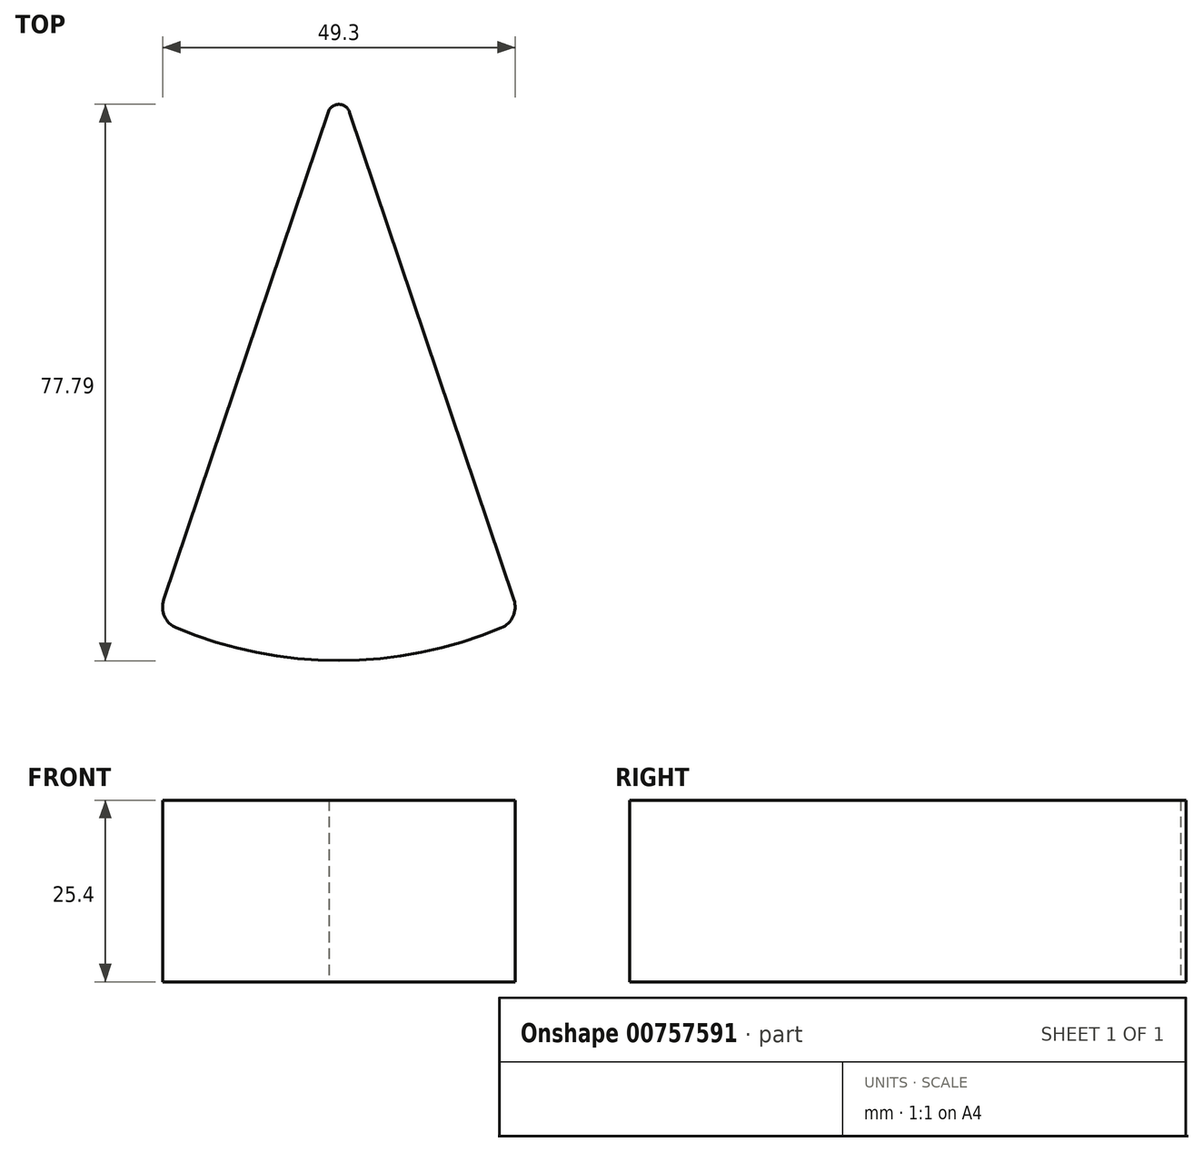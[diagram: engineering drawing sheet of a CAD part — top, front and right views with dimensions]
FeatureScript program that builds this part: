
annotation { "Feature Type Name" : "Feature", "Feature Type Description" : "" }
export const myFeature = defineFeature(function(context is Context, id is Id, definition is map)
    precondition{}
    {
        {
            var Q0;
            Q0=qCreatedBy(makeId("Top.planeOp"),FACE);
            var sketch = newSketch(context, id + "F0", { "sketchPlane" : qUnion([Q0])});
            skLineSegment(sketch, "E0", {"start": v(-26.76, 71.23) * mm, "end": v(-49.88, 2.73) * mm});
            skLineSegment(sketch, "E1", {"start": v(-23.9, 70.92) * mm, "end": v(-0.92, 2.73) * mm});
            skPoint(sketch, "E2.visualSharp", {"position": v(-25.38, 75.32) * mm});
            skArc(sketch, "E2.filletArc", {"start": v(-23.9, 70.92) * mm, "mid": v(-25.23, 72) * mm, "end": v(-26.76, 71.23) * mm});
            skLineSegment(sketch, "E3", {"start": v(-50.8, 0) * mm, "end": v(0, 0) * mm, "construction": true});
            skLineSegment(sketch, "E4", {"start": v(-25.4, 70.41) * mm, "end": v(-25.4, 0) * mm, "construction": true});
            skArc(sketch, "E5", {"start": v(-48.1, -1.21) * mm, "mid": v(-25.4, -5.79) * mm, "end": v(-2.7, -1.21) * mm});
            skPoint(sketch, "E6.visualSharp", {"position": v(-50.8, 0) * mm});
            skArc(sketch, "E6.filletArc", {"start": v(-49.88, 2.73) * mm, "mid": v(-49.77, 0.4) * mm, "end": v(-48.1, -1.21) * mm});
            skPoint(sketch, "E7.visualSharp", {"position": v(0, 0) * mm});
            skArc(sketch, "E7.filletArc", {"start": v(-2.7, -1.21) * mm, "mid": v(-1.03, 0.4) * mm, "end": v(-0.92, 2.73) * mm});
            skSolve(sketch);
        }
        {
            var Q0;
            Q0 = qSketchRegion(id + "F0", true);
            extrude(context, id + "F1", {"entities" : qUnion([Q0]), "depth" : 25.4 * mm, "offsetDistance" : 25.4 * mm});
        }
    });
